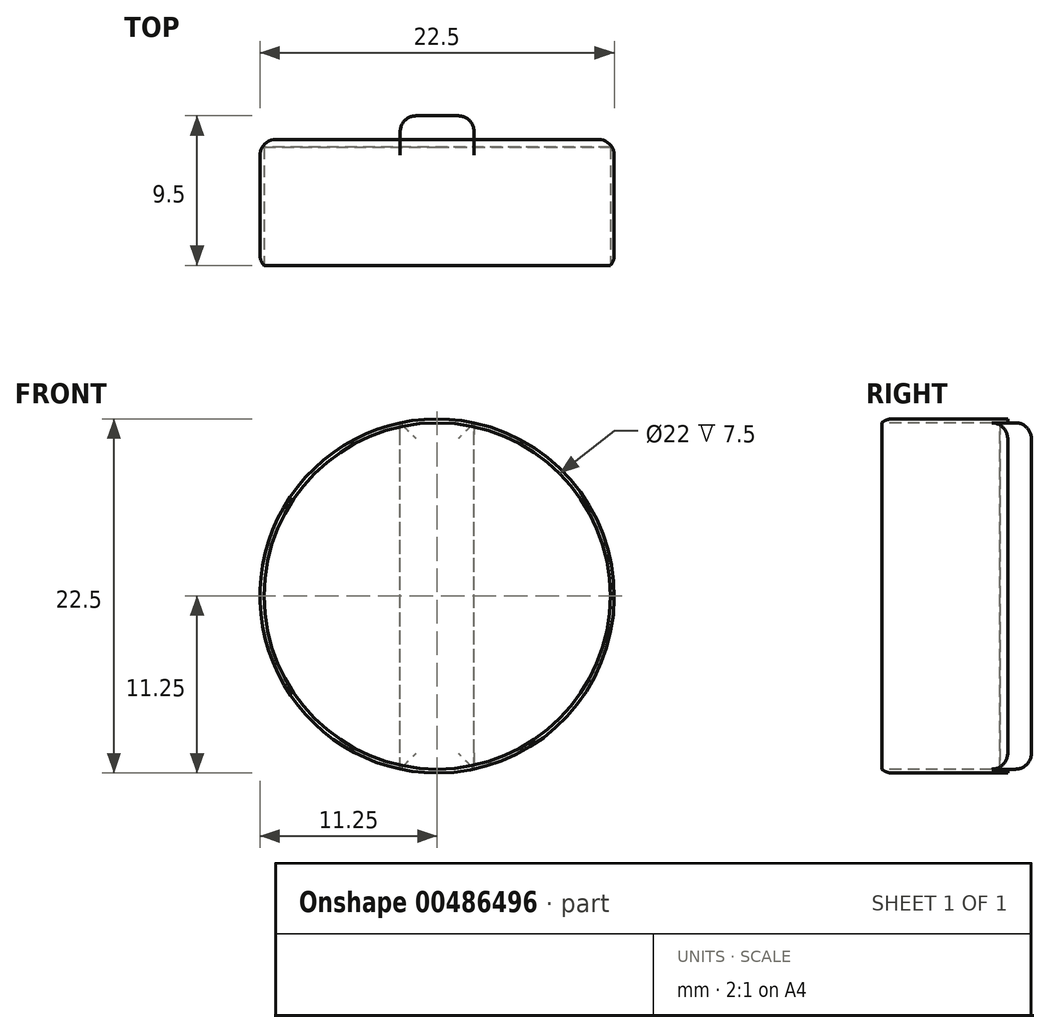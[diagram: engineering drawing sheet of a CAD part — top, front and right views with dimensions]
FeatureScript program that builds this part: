
annotation { "Feature Type Name" : "Feature", "Feature Type Description" : "" }
export const myFeature = defineFeature(function(context is Context, id is Id, definition is map)
    precondition{}
    {
        {
            var Q0;
            Q0=qCreatedBy(makeId("Front.planeOp"),FACE);
            var sketch = newSketch(context, id + "F0", { "sketchPlane" : qUnion([Q0])});
            skCircle(sketch, "E0", {"center": v(0, 0) * mm, "radius": 11.25 * mm});
            skSolve(sketch);
        }
        {
            var Q0;
            Q0 = qSketchRegion(id + "F0", true);
            extrude(context, id + "F1", {"entities" : qUnion([Q0]), "depth" : 8 * mm});
        }
        {
            var Q0;
            Q0=makeQuery(id+"F1.opExtrude","CAP_FACE",FACE,{"disambiguationData":[OSD([sQuery(id+"F0.wireOp",EDGE,"E0")])],"isStart":false});
            var sketch = newSketch(context, id + "F2", { "sketchPlane" : qUnion([Q0])});
            skCircle(sketch, "E1", {"center": v(0, 0) * mm, "radius": 11 * mm});
            skSolve(sketch);
        }
        {
            var Q0;
            Q0 = qSketchRegion(id + "F2", true);
            extrude(context, id + "F3", {"entities" : qUnion([Q0]), "operationType" : NewBodyOperationType.REMOVE, "oppositeDirection" : true, "depth" : 7.5 * mm});
        }
        {
            var Q0;
            Q0=makeQuery(id+"F1.opExtrude","CAP_FACE",FACE,{"disambiguationData":[OSD([sQuery(id+"F0.wireOp",EDGE,"E0")])],"isStart":true});
            var sketch = newSketch(context, id + "F4", { "sketchPlane" : qUnion([Q0])});
            skLineSegment(sketch, "E2.bottom", {"start": v(2.35, -11) * mm, "end": v(-2.35, -11) * mm});
            skLineSegment(sketch, "E2.top", {"start": v(2.35, 11) * mm, "end": v(-2.35, 11) * mm});
            skLineSegment(sketch, "E2.left", {"start": v(2.35, -11) * mm, "end": v(2.35, 11) * mm});
            skLineSegment(sketch, "E2.right", {"start": v(-2.35, -11) * mm, "end": v(-2.35, 11) * mm});
            skPoint(sketch, "E2.middle", {"position": v(0, 0) * mm});
            skSolve(sketch);
        }
        {
            var Q0;
            Q0 = qSketchRegion(id + "F4", true);
            extrude(context, id + "F5", {"entities" : qUnion([Q0]), "operationType" : NewBodyOperationType.ADD, "depth" : 1.5 * mm});
        }
        {
            var Q0;
            Q0=makeQuery(id+"F5.opExtrude","CAP_FACE",FACE,{"disambiguationData":[OSD([sQuery(id+"F4.wireOp",EDGE,"E2.bottom"),sQuery(id+"F4.wireOp",EDGE,"E2.top"),sQuery(id+"F4.wireOp",EDGE,"E2.left"),sQuery(id+"F4.wireOp",EDGE,"E2.right")])],"isStart":false});
            var Q1;
            Q1=makeQuery(id+"F1.opExtrude","SWEPT_FACE",FACE,{"disambiguationData":[OSD([sQuery(id+"F0.wireOp",EDGE,"E0")])]});
            fillet(context, id + "F6", {"entities" : qUnion([Q0, Q1]), "radius" : 1 * mm, "tangentPropagation" : true, "allowEdgeOverflow" : false});
        }
    });
